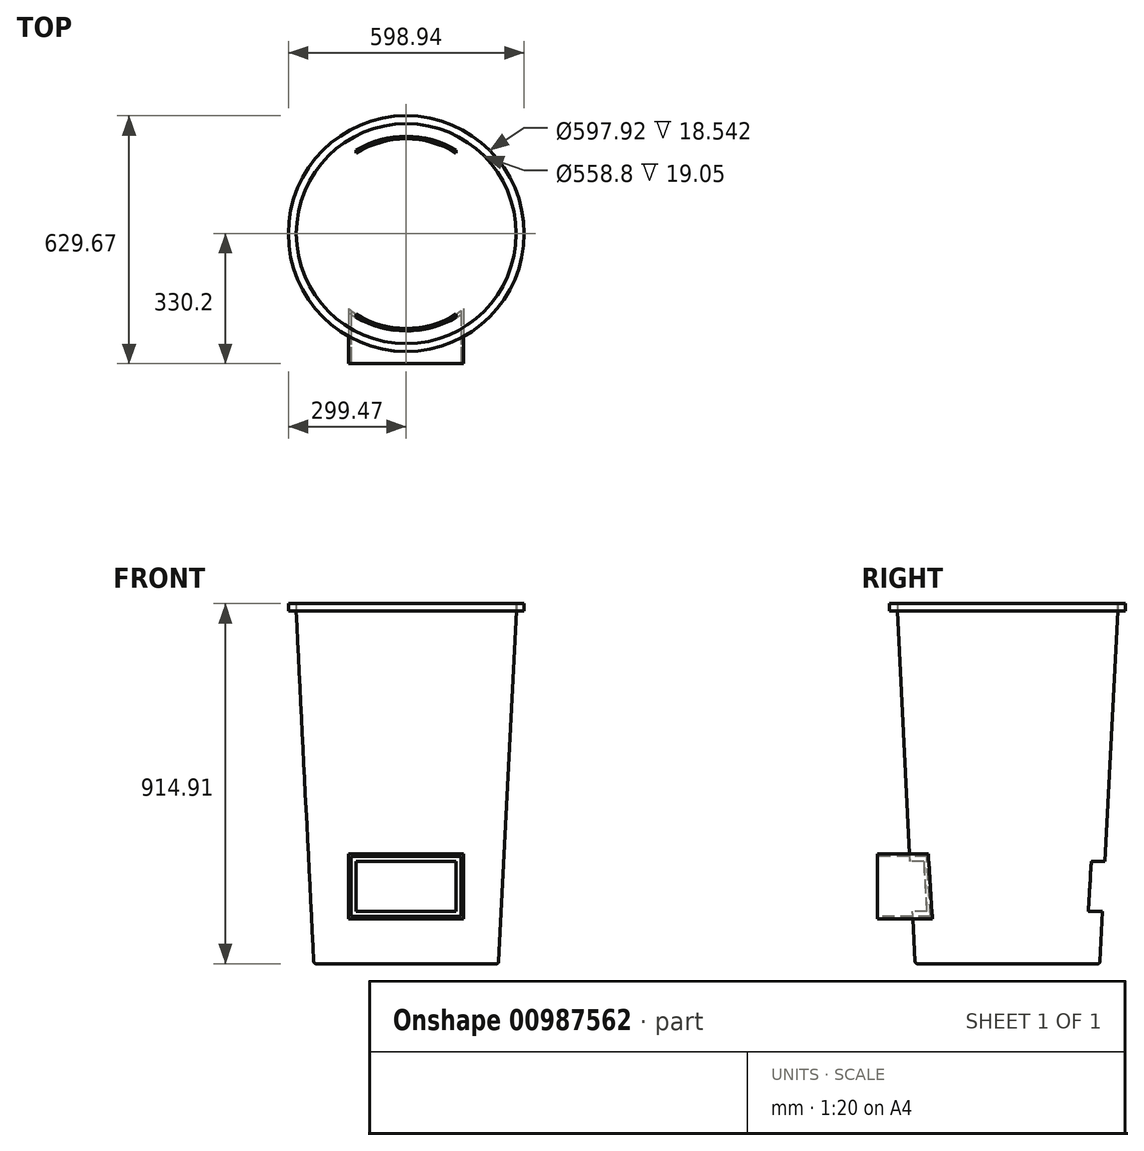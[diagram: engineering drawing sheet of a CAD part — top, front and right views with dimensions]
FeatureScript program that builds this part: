
annotation { "Feature Type Name" : "Feature", "Feature Type Description" : "" }
export const myFeature = defineFeature(function(context is Context, id is Id, definition is map)
    precondition{}
    {
        {
            var Q0;
            Q0=qCreatedBy(makeId("Front.planeOp"),FACE);
            var sketch = newSketch(context, id + "F0", { "sketchPlane" : qUnion([Q0])});
            skLineSegment(sketch, "E0", {"start": v(0, 0) * mm, "end": v(228.6, 0) * mm});
            skLineSegment(sketch, "E1", {"start": v(234.94, 6.03) * mm, "end": v(279.9, 895.86) * mm});
            skLineSegment(sketch, "E2", {"start": v(279.9, 895.86) * mm, "end": v(279.9, 914.4) * mm});
            skLineSegment(sketch, "E3", {"start": v(279.9, 914.4) * mm, "end": v(298.96, 914.4) * mm});
            skLineSegment(sketch, "E4", {"start": v(298.96, 914.4) * mm, "end": v(298.96, 895.86) * mm});
            skLineSegment(sketch, "E5", {"start": v(298.96, 895.86) * mm, "end": v(299.47, 895.86) * mm});
            skLineSegment(sketch, "E6", {"start": v(299.47, 895.86) * mm, "end": v(299.47, 914.9) * mm});
            skLineSegment(sketch, "E7", {"start": v(299.47, 914.9) * mm, "end": v(279.4, 914.9) * mm});
            skLineSegment(sketch, "E8", {"start": v(279.4, 914.9) * mm, "end": v(279.4, 895.86) * mm});
            skLineSegment(sketch, "E9", {"start": v(279.4, 895.86) * mm, "end": v(234.46, 6.54) * mm});
            skLineSegment(sketch, "E10", {"start": v(228.12, 0.5) * mm, "end": v(0, 0.5) * mm});
            skLineSegment(sketch, "E11", {"start": v(0, 0.5) * mm, "end": v(0, 0) * mm});
            skPoint(sketch, "E12.visualSharp", {"position": v(234.64, 0) * mm});
            skArc(sketch, "E12.filletArc", {"start": v(228.6, 0) * mm, "mid": v(232.98, 1.75) * mm, "end": v(234.94, 6.03) * mm});
            skPoint(sketch, "E13.visualSharp", {"position": v(234.15, 0.5) * mm});
            skArc(sketch, "E13.filletArc", {"start": v(228.12, 0.5) * mm, "mid": v(232.5, 2.26) * mm, "end": v(234.46, 6.54) * mm});
            skSolve(sketch);
        }
        {
            var Q0;
            Q0=qCreatedBy(makeId("Front.planeOp"),FACE);
            var sketch = newSketch(context, id + "F1", { "sketchPlane" : qUnion([Q0])});
            skLineSegment(sketch, "E14", {"start": v(0, 0) * mm, "end": v(0, 56.42) * mm});
            skSolve(sketch);
        }
        {
            var Q0;
            Q0 = qSketchRegion(id + "F0", true);
            var Q1;
            Q1=sQuery(id+"F1.wireOp",EDGE,"E14");
            revolve(context, id + "F2", {"surfaceOperationType" : NewSurfaceOperationType.NEW, "entities" : qUnion([Q0]), "axis" : qUnion([Q1]), "revolveType" : RevolveType.FULL});
        }
        {
            var Q0;
            Q0=qCreatedBy(makeId("Front.planeOp"),FACE);
            var sketch = newSketch(context, id + "F3", { "sketchPlane" : qUnion([Q0])});
            skLineSegment(sketch, "E15.bottom", {"start": v(-127, 133.03) * mm, "end": v(127, 133.03) * mm});
            skLineSegment(sketch, "E15.top", {"start": v(-127, 260.03) * mm, "end": v(127, 260.03) * mm});
            skLineSegment(sketch, "E15.left", {"start": v(-127, 133.03) * mm, "end": v(-127, 260.03) * mm});
            skLineSegment(sketch, "E15.right", {"start": v(127, 133.03) * mm, "end": v(127, 260.03) * mm});
            skSolve(sketch);
        }
        {
            var Q0;
            Q0 = qSketchRegion(id + "F3", true);
            extrude(context, id + "F4", {"entities" : qUnion([Q0]), "operationType" : NewBodyOperationType.REMOVE, "endBound" : BoundingType.THROUGH_ALL, "oppositeDirection" : true, "depth" : 508 * mm, "offsetDistance" : 25.4 * mm});
        }
        {
            var Q0;
            Q0 = qSketchRegion(id + "F3", true);
            extrude(context, id + "F5", {"entities" : qUnion([Q0]), "operationType" : NewBodyOperationType.REMOVE, "endBound" : BoundingType.THROUGH_ALL, "depth" : 25.4 * mm, "offsetDistance" : 25.4 * mm});
        }
        {
            var Q0;
            Q0=qCreatedBy(makeId("Front.planeOp"),FACE);
            cPlane(context, id + "F6", {"entities" : qUnion([Q0]), "cplaneType" : CPlaneType.OFFSET, "offset" : 330.2 * mm, "width" : 152.4 * mm, "height" : 152.4 * mm});
        }
        {
            var Q0;
            Q0=qCreatedBy(id+"F6.planeOp",FACE);
            var sketch = newSketch(context, id + "F7", { "sketchPlane" : qUnion([Q0])});
            skLineSegment(sketch, "E16.bottom", {"start": v(-139.7, 272.73) * mm, "end": v(139.7, 272.73) * mm});
            skLineSegment(sketch, "E16.top", {"start": v(-139.7, 120.33) * mm, "end": v(139.7, 120.33) * mm});
            skLineSegment(sketch, "E16.left", {"start": v(-139.7, 272.73) * mm, "end": v(-139.7, 120.33) * mm});
            skLineSegment(sketch, "E16.right", {"start": v(139.7, 272.73) * mm, "end": v(139.7, 120.33) * mm});
            skLineSegment(sketch, "E17.bottom", {"start": v(-146.05, 279.08) * mm, "end": v(146.05, 279.08) * mm});
            skLineSegment(sketch, "E17.top", {"start": v(-146.05, 113.98) * mm, "end": v(146.05, 113.98) * mm});
            skLineSegment(sketch, "E17.left", {"start": v(-146.05, 279.08) * mm, "end": v(-146.05, 113.98) * mm});
            skLineSegment(sketch, "E17.right", {"start": v(146.05, 279.08) * mm, "end": v(146.05, 113.98) * mm});
            skSolve(sketch);
        }
        {
            var Q0;
            Q0 = qSketchRegion(id + "F7", true);
            extrude(context, id + "F8", {"entities" : qUnion([Q0]), "operationType" : NewBodyOperationType.ADD, "endBound" : BoundingType.UP_TO_NEXT, "oppositeDirection" : true, "depth" : 25.4 * mm, "offsetDistance" : 25.4 * mm});
        }
    });
